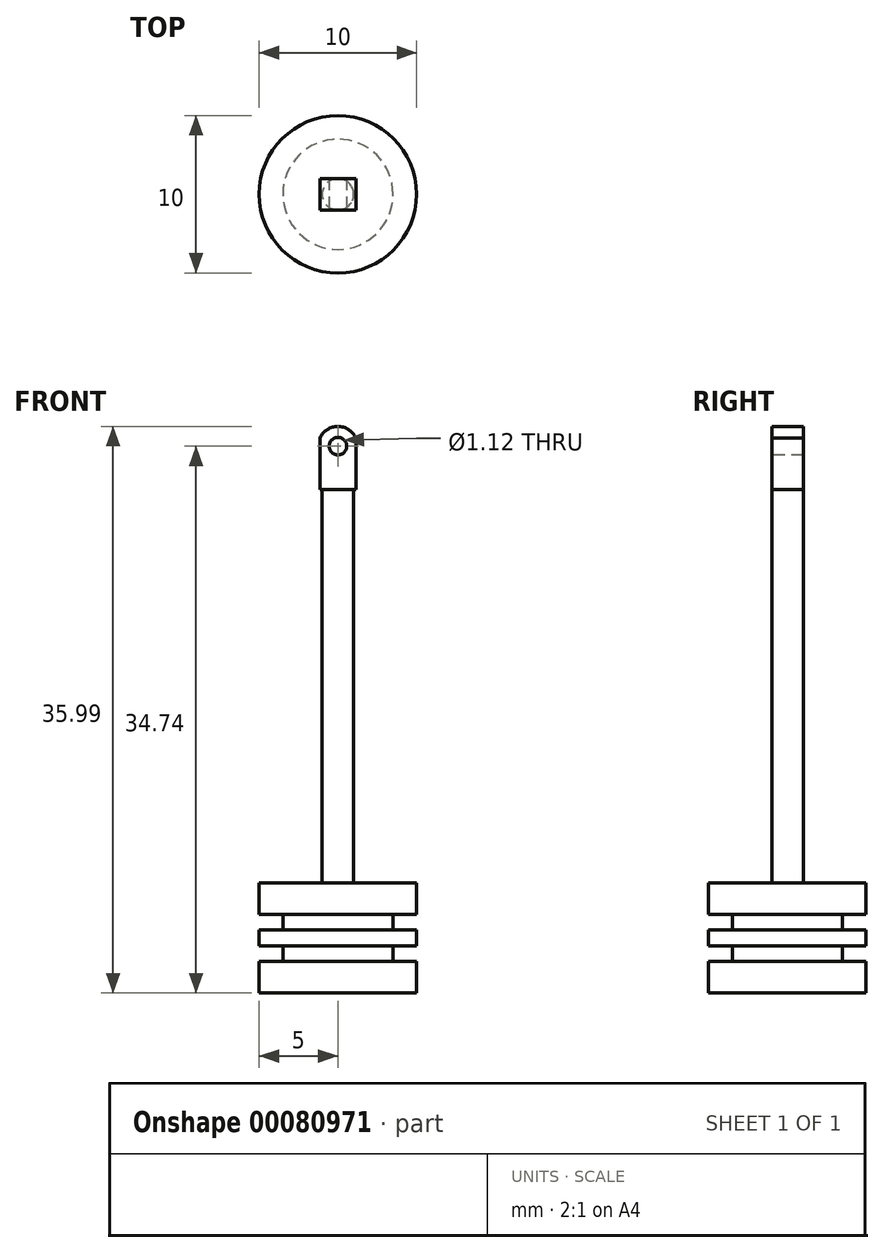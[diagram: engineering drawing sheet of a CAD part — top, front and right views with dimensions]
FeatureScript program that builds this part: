
annotation { "Feature Type Name" : "Feature", "Feature Type Description" : "" }
export const myFeature = defineFeature(function(context is Context, id is Id, definition is map)
    precondition{}
    {
        {
            var Q0;
            Q0=qCreatedBy(makeId("Top.planeOp"),FACE);
            var sketch = newSketch(context, id + "F0", { "sketchPlane" : qUnion([Q0])});
            skCircle(sketch, "E0", {"center": v(0, 0) * mm, "radius": 5 * mm});
            skSolve(sketch);
        }
        {
            var Q0;
            Q0=makeQuery(id+"F0.imprint","IMPRINT",FACE,{"disambiguationData":[TD([[makeQuery(id+"F0.imprint","IMPRINT",EDGE,{"derivedFrom":sQuery(id+"F0.wireOp",EDGE,"E0")}),1.0]])]});
            extrude(context, id + "F1", {"entities" : qUnion([Q0]), "depth" : 2 * mm});
        }
        {
            var Q0;
            Q0=makeQuery(id+"F1.opExtrude","CAP_FACE",FACE,{"disambiguationData":[OSD([sQuery(id+"F0.wireOp",EDGE,"E0")])],"isStart":false});
            var sketch = newSketch(context, id + "F2", { "sketchPlane" : qUnion([Q0])});
            skCircle(sketch, "E1", {"center": v(0, 0) * mm, "radius": 3.5 * mm});
            skSolve(sketch);
        }
        {
            var Q0;
            Q0=makeQuery(id+"F2.imprint","IMPRINT",FACE,{"disambiguationData":[TD([[makeQuery(id+"F2.imprint","IMPRINT",EDGE,{"derivedFrom":sQuery(id+"F2.wireOp",EDGE,"E1")}),1.0]])]});
            extrude(context, id + "F3", {"entities" : qUnion([Q0]), "operationType" : NewBodyOperationType.ADD, "depth" : 1 * mm});
        }
        {
            var Q0;
            Q0=makeQuery(id+"F3.opExtrude","CAP_FACE",FACE,{"disambiguationData":[OSD([sQuery(id+"F2.wireOp",EDGE,"E1")])],"isStart":false});
            var sketch = newSketch(context, id + "F4", { "sketchPlane" : qUnion([Q0])});
            skCircle(sketch, "E2", {"center": v(0, 0) * mm, "radius": 5 * mm});
            skSolve(sketch);
        }
        {
            var Q0;
            Q0=makeQuery(id+"F4.imprint","IMPRINT",FACE,{"disambiguationData":[TD([[makeQuery(id+"F4.imprint","IMPRINT",EDGE,{"derivedFrom":sQuery(id+"F4.wireOp",EDGE,"E2")}),1.0]])]});
            var Q1;
            Q1=makeQuery(id+"F4.imprint","IMPRINT",FACE,{"disambiguationData":[TD([[makeQuery(id+"F4.imprint","IMPRINT",EDGE,{"derivedFrom":makeQuery(id+"F3.opExtrude","CAP_EDGE",EDGE,{"disambiguationData":[OSD([sQuery(id+"F2.wireOp",EDGE,"E1")])],"isStart":false})}),1.0]])]});
            extrude(context, id + "F5", {"entities" : qUnion([Q0, Q1]), "depth" : 1 * mm});
        }
        {
            var Q0;
            Q0=makeQuery(id+"F5.opExtrude","CAP_FACE",FACE,{"disambiguationData":[OSD([sQuery(id+"F4.wireOp",EDGE,"E2")])],"isStart":false});
            var sketch = newSketch(context, id + "F6", { "sketchPlane" : qUnion([Q0])});
            skCircle(sketch, "E3", {"center": v(0, 0) * mm, "radius": 3.5 * mm});
            skSolve(sketch);
        }
        {
            var Q0;
            Q0=makeQuery(id+"F6.imprint","IMPRINT",FACE,{"disambiguationData":[TD([[makeQuery(id+"F6.imprint","IMPRINT",EDGE,{"derivedFrom":sQuery(id+"F6.wireOp",EDGE,"E3")}),1.0]])]});
            extrude(context, id + "F7", {"entities" : qUnion([Q0]), "operationType" : NewBodyOperationType.ADD, "depth" : 1 * mm});
        }
        {
            var Q0;
            Q0=makeQuery(id+"F7.opExtrude","CAP_FACE",FACE,{"disambiguationData":[OSD([sQuery(id+"F6.wireOp",EDGE,"E3")])],"isStart":false});
            var sketch = newSketch(context, id + "F8", { "sketchPlane" : qUnion([Q0])});
            skCircle(sketch, "E4", {"center": v(0, 0) * mm, "radius": 5 * mm});
            skSolve(sketch);
        }
        {
            var Q0;
            Q0=makeQuery(id+"F8.imprint","IMPRINT",FACE,{"disambiguationData":[TD([[makeQuery(id+"F8.imprint","IMPRINT",EDGE,{"derivedFrom":sQuery(id+"F8.wireOp",EDGE,"E4")}),1.0]])]});
            var Q1;
            Q1=makeQuery(id+"F8.imprint","IMPRINT",FACE,{"disambiguationData":[TD([[makeQuery(id+"F8.imprint","IMPRINT",EDGE,{"derivedFrom":makeQuery(id+"F7.opExtrude","CAP_EDGE",EDGE,{"disambiguationData":[OSD([sQuery(id+"F6.wireOp",EDGE,"E3")])],"isStart":false})}),1.0]])]});
            extrude(context, id + "F9", {"entities" : qUnion([Q0, Q1]), "operationType" : NewBodyOperationType.ADD, "depth" : 2 * mm});
        }
        {
            var Q0;
            Q0=makeQuery(id+"F9.opExtrude","CAP_FACE",FACE,{"disambiguationData":[OSD([sQuery(id+"F8.wireOp",EDGE,"E4")])],"isStart":false});
            var sketch = newSketch(context, id + "F10", { "sketchPlane" : qUnion([Q0])});
            skCircle(sketch, "E5", {"center": v(0, 0) * mm, "radius": 1 * mm});
            skSolve(sketch);
        }
        {
            var Q0;
            Q0=makeQuery(id+"F10.imprint","IMPRINT",FACE,{"disambiguationData":[TD([[makeQuery(id+"F10.imprint","IMPRINT",EDGE,{"derivedFrom":sQuery(id+"F10.wireOp",EDGE,"E5")}),1.0]])]});
            extrude(context, id + "F11", {"entities" : qUnion([Q0]), "operationType" : NewBodyOperationType.ADD, "depth" : 25 * mm});
        }
        {
            var Q0;
            Q0=makeQuery(id+"F11.opExtrude","CAP_FACE",FACE,{"disambiguationData":[OSD([sQuery(id+"F10.wireOp",EDGE,"E5")])],"isStart":false});
            var sketch = newSketch(context, id + "F12", { "sketchPlane" : qUnion([Q0])});
            skLineSegment(sketch, "E6.bottom", {"start": v(-1.13, 1) * mm, "end": v(1.13, 1) * mm});
            skLineSegment(sketch, "E6.top", {"start": v(-1.13, -1) * mm, "end": v(1.13, -1) * mm});
            skLineSegment(sketch, "E6.left", {"start": v(-1.13, 1) * mm, "end": v(-1.13, -1) * mm});
            skLineSegment(sketch, "E6.right", {"start": v(1.13, 1) * mm, "end": v(1.13, -1) * mm});
            skPoint(sketch, "E6.middle", {"position": v(0, 0) * mm});
            skSolve(sketch);
        }
        {
            var Q0;
            {var subQ0=sQuery(id+"F12.wireOp",EDGE,"E6.right");Q0=makeQuery(id+"F12.imprint","IMPRINT",FACE,{"disambiguationData":[TD([[makeQuery(id+"F12.imprint","IMPRINT",EDGE,{"derivedFrom":subQ0}),-1.0]])]});}
            var Q1;
            {var subQ0=sQuery(id+"F12.wireOp",EDGE,"E6.left");Q1=makeQuery(id+"F12.imprint","IMPRINT",FACE,{"disambiguationData":[TD([[makeQuery(id+"F12.imprint","IMPRINT",EDGE,{"derivedFrom":subQ0}),1.0]])]});}
            var Q2;
            {var subQ0=makeQuery(id+"F11.opExtrude","CAP_EDGE",EDGE,{"disambiguationData":[OSD([sQuery(id+"F10.wireOp",EDGE,"E5")])],"isStart":false});var subQ1=makeQuery(id+"F12.imprint","INTERSECT",VERTEX,{"derivedFrom":[subQ0,sQuery(id+"F12.wireOp",EDGE,"E6.bottom")]});Q2=makeQuery(id+"F12.imprint","IMPRINT",FACE,{"disambiguationData":[TD([[makeQuery(id+"F12.imprint","IMPRINT",EDGE,{"disambiguationData":[TD([[subQ1,-1.0]])],"derivedFrom":subQ0}),1.0]])]});}
            extrude(context, id + "F13", {"entities" : qUnion([Q0, Q1, Q2]), "operationType" : NewBodyOperationType.ADD, "depth" : 4 * mm});
        }
        {
            var Q0;
            Q0=makeQuery(id+"F13.opExtrude","SWEPT_FACE",FACE,{"disambiguationData":[OSD([sQuery(id+"F12.wireOp",EDGE,"E6.top")])]});
            var sketch = newSketch(context, id + "F14", { "sketchPlane" : qUnion([Q0])});
            skPoint(sketch, "E7", {"position": v(0, 36) * mm});
            skArc(sketch, "E8", {"start": v(1.25, 34.72) * mm, "mid": v(0, 36) * mm, "end": v(-1.25, 34.73) * mm});
            skLineSegment(sketch, "E9", {"start": v(-1.25, 34.73) * mm, "end": v(-1.25, 32) * mm});
            skLineSegment(sketch, "E10", {"start": v(1.25, 32) * mm, "end": v(1.25, 34.72) * mm});
            skLineSegment(sketch, "E11", {"start": v(-1.13, 32) * mm, "end": v(-11.06, -1.5) * mm});
            skLineSegment(sketch, "E12", {"start": v(-11.06, -1.5) * mm, "end": v(-0.26, -3.17) * mm});
            skLineSegment(sketch, "E13", {"start": v(-0.26, -3.17) * mm, "end": v(14.62, 1) * mm});
            skLineSegment(sketch, "E14", {"start": v(14.62, 1) * mm, "end": v(6.64, 14.44) * mm});
            skLineSegment(sketch, "E15", {"start": v(6.64, 14.44) * mm, "end": v(1.25, 32) * mm});
            skSolve(sketch);
        }
        {
            var Q0;
            {var subQ0=sQuery(id+"F14.wireOp",EDGE,"E10");Q0=makeQuery(id+"F14.imprint","IMPRINT",FACE,{"disambiguationData":[TD([[makeQuery(id+"F14.imprint","IMPRINT",EDGE,{"derivedFrom":subQ0}),1.0]])]});}
            var Q1;
            {var subQ2=sQuery(id+"F12.wireOp",EDGE,"E6.left");var subQ3=sQuery(id+"F12.wireOp",EDGE,"E6.top");var subQ8=makeQuery(id+"F13.opExtrude","SWEPT_EDGE",EDGE,{"disambiguationData":[OSD([subQ3,subQ2])]});var subQ9=sQuery(id+"F14.wireOp",EDGE,"E8");var subQ10=makeQuery(id+"F14.imprint","INTERSECT",VERTEX,{"derivedFrom":[subQ8,subQ9]});Q1=makeQuery(id+"F14.imprint","IMPRINT",FACE,{"disambiguationData":[TD([[makeQuery(id+"F14.imprint","IMPRINT",EDGE,{"disambiguationData":[TD([[subQ10,1.0]])],"derivedFrom":subQ9}),1.0]])]});}
            extrude(context, id + "F15", {"entities" : qUnion([Q0, Q1]), "operationType" : NewBodyOperationType.INTERSECT, "endBound" : BoundingType.SYMMETRIC, "oppositeDirection" : true, "depth" : 25 * mm});
        }
        {
            var Q0;
            Q0=makeQuery(id+"F13.opExtrude","SWEPT_FACE",FACE,{"disambiguationData":[OSD([sQuery(id+"F12.wireOp",EDGE,"E6.top")])]});
            var sketch = newSketch(context, id + "F16", { "sketchPlane" : qUnion([Q0])});
            skLineSegment(sketch, "E16", {"start": v(-1.13, 35.26) * mm, "end": v(1.13, 35.26) * mm, "construction": true});
            skLineSegment(sketch, "E17", {"start": v(0, 36) * mm, "end": v(0, 32) * mm, "construction": true});
            skCircle(sketch, "E18", {"center": v(0, 34.74) * mm, "radius": 0.56 * mm});
            skSolve(sketch);
        }
        {
            var Q0;
            Q0=makeQuery(id+"F16.imprint","IMPRINT",FACE,{"disambiguationData":[TD([[makeQuery(id+"F16.imprint","IMPRINT",EDGE,{"derivedFrom":sQuery(id+"F16.wireOp",EDGE,"E18")}),1.0]])]});
            extrude(context, id + "F17", {"entities" : qUnion([Q0]), "operationType" : NewBodyOperationType.REMOVE, "oppositeDirection" : true, "depth" : 25 * mm});
        }
    });
